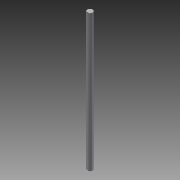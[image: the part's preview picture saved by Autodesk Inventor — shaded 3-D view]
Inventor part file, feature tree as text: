
AUTODESK INVENTOR PART (.ipt)
format: ipt  version: 2013 (Build 170138000, 138)  size: 70,656 bytes
history: native  units: in
note: dims shown in document units (in); Inventor stores cm internally (conversion verified against a paired STEP export)
features: extrude x1, sketch x1
ambient origin geometry x8: Origin, YZ Plane, XZ Plane, XY Plane, X Axis, Y Axis, Z Axis, Center Point
bodies: Solid1 (feature_tree)
feature tree (2):
  extrude  "Extrusion1"  Depth=0.0787in
  sketch  "Sketch1"  dims[d0=0.315in d1=0.0787in d2=0.0394in d3=0.0394in d4=8.0in d5=0.0in]
